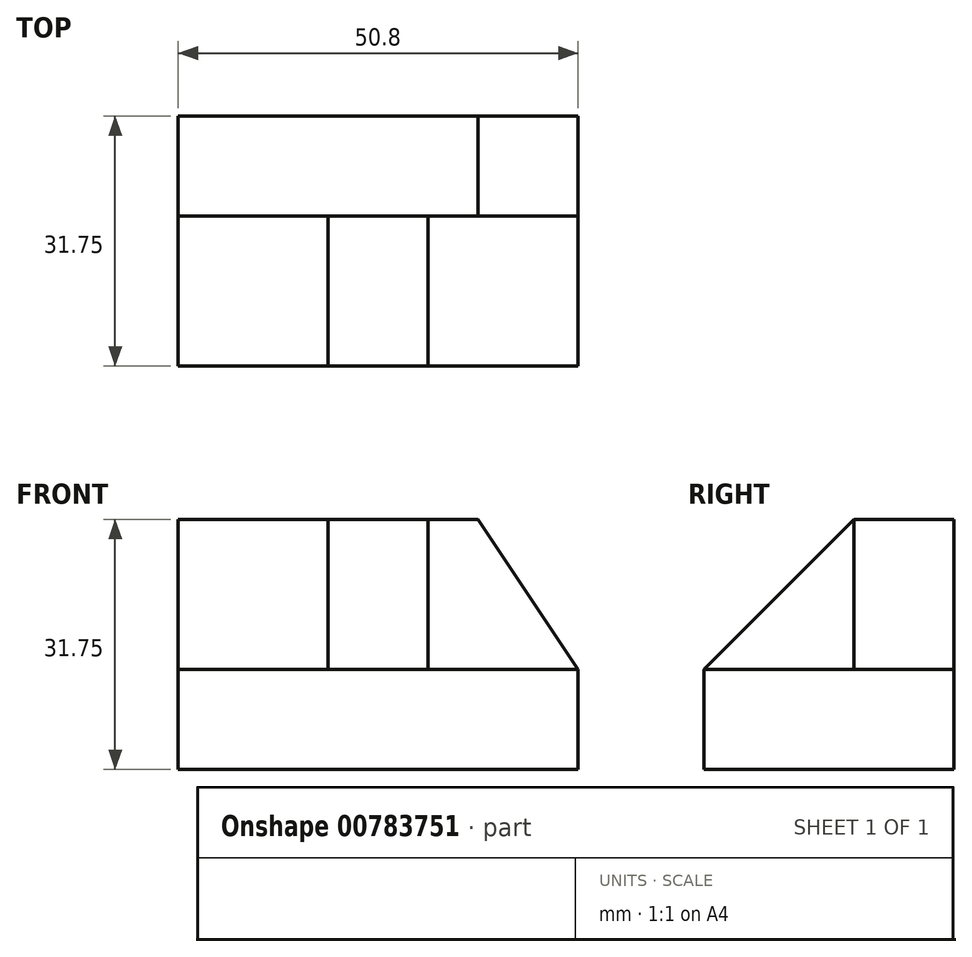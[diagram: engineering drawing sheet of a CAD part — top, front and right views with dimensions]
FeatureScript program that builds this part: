
annotation { "Feature Type Name" : "Feature", "Feature Type Description" : "" }
export const myFeature = defineFeature(function(context is Context, id is Id, definition is map)
    precondition{}
    {
        {
            var Q0;
            Q0=qCreatedBy(makeId("Front.planeOp"),FACE);
            var sketch = newSketch(context, id + "F0", { "sketchPlane" : qUnion([Q0])});
            skLineSegment(sketch, "E0", {"start": v(0, 0) * mm, "end": v(50.8, 0) * mm});
            skLineSegment(sketch, "E1", {"start": v(50.8, 0) * mm, "end": v(50.8, 31.75) * mm});
            skLineSegment(sketch, "E2", {"start": v(50.8, 31.75) * mm, "end": v(0, 31.75) * mm});
            skLineSegment(sketch, "E3", {"start": v(0, 31.75) * mm, "end": v(0, 0) * mm});
            skSolve(sketch);
        }
        {
            var Q0;
            Q0=makeQuery(id+"F0.imprint","IMPRINT",FACE,{"disambiguationData":[TD([[makeQuery(id+"F0.imprint","IMPRINT",EDGE,{"derivedFrom":sQuery(id+"F0.wireOp",EDGE,"E0")}),1.0]])]});
            extrude(context, id + "F1", {"entities" : qUnion([Q0]), "depth" : 31.75 * mm, "offsetDistance" : 25.4 * mm});
        }
        {
            var Q0;
            Q0=makeQuery(id+"F1.opExtrude","SWEPT_FACE",FACE,{"disambiguationData":[OSD([sQuery(id+"F0.wireOp",EDGE,"E3")])]});
            var sketch = newSketch(context, id + "F2", { "sketchPlane" : qUnion([Q0])});
            skLineSegment(sketch, "E4", {"start": v(0, 31.75) * mm, "end": v(12.7, 31.75) * mm});
            skLineSegment(sketch, "E5", {"start": v(31.75, 0) * mm, "end": v(31.75, 12.7) * mm});
            skLineSegment(sketch, "E6", {"start": v(31.75, 12.7) * mm, "end": v(12.7, 12.7) * mm});
            skLineSegment(sketch, "E7", {"start": v(12.7, 12.7) * mm, "end": v(12.7, 31.75) * mm});
            skSolve(sketch);
        }
        {
            var Q0;
            {var subQ0=sQuery(id+"F2.wireOp",EDGE,"E6");Q0=makeQuery(id+"F2.imprint","IMPRINT",FACE,{"disambiguationData":[TD([[makeQuery(id+"F2.imprint","IMPRINT",EDGE,{"derivedFrom":subQ0}),-1.0]])]});}
            extrude(context, id + "F3", {"entities" : qUnion([Q0]), "operationType" : NewBodyOperationType.REMOVE, "oppositeDirection" : true, "depth" : 19.05 * mm, "offsetDistance" : 25.4 * mm});
        }
        {
            var Q0;
            Q0=makeQuery(id+"F1.opExtrude","SWEPT_FACE",FACE,{"disambiguationData":[OSD([sQuery(id+"F0.wireOp",EDGE,"E1")])]});
            var sketch = newSketch(context, id + "F4", { "sketchPlane" : qUnion([Q0])});
            skLineSegment(sketch, "E8", {"start": v(-31.75, 0) * mm, "end": v(-31.75, 12.7) * mm});
            skLineSegment(sketch, "E9", {"start": v(-31.75, 12.7) * mm, "end": v(-12.7, 12.7) * mm});
            skLineSegment(sketch, "E10", {"start": v(0, 31.75) * mm, "end": v(0, 31.75) * mm});
            skLineSegment(sketch, "E11", {"start": v(0, 31.75) * mm, "end": v(-12.7, 31.75) * mm});
            skLineSegment(sketch, "E12", {"start": v(-12.7, 31.75) * mm, "end": v(-12.7, 12.7) * mm});
            skSolve(sketch);
        }
        {
            var Q0;
            {var subQ0=sQuery(id+"F4.wireOp",EDGE,"E9");Q0=makeQuery(id+"F4.imprint","IMPRINT",FACE,{"disambiguationData":[TD([[makeQuery(id+"F4.imprint","IMPRINT",EDGE,{"derivedFrom":subQ0}),1.0]])]});}
            extrude(context, id + "F5", {"entities" : qUnion([Q0]), "operationType" : NewBodyOperationType.REMOVE, "oppositeDirection" : true, "depth" : 19.05 * mm, "offsetDistance" : 25.4 * mm});
        }
        {
            var Q0;
            Q0=makeQuery(id+"F5.boolean.opBoolean","COPY",FACE,{"derivedFrom":makeQuery(id+"F5.opExtrude","CAP_FACE",FACE,{"disambiguationData":[OSD([sQuery(id+"F0.wireOp",EDGE,"E1"),sQuery(id+"F0.wireOp",EDGE,"E2"),sQuery(id+"F4.wireOp",EDGE,"E9"),sQuery(id+"F4.wireOp",EDGE,"E12")])],"isStart":false})});
            var sketch = newSketch(context, id + "F6", { "sketchPlane" : qUnion([Q0])});
            skLineSegment(sketch, "E13", {"start": v(-12.7, 31.75) * mm, "end": v(-31.75, 12.7) * mm});
            skSolve(sketch);
        }
        {
            var Q0;
            Q0=makeQuery(id+"F6.imprint","IMPRINT",FACE,{"disambiguationData":[TD([[makeQuery(id+"F6.imprint","IMPRINT",EDGE,{"derivedFrom":sQuery(id+"F6.wireOp",EDGE,"E13")}),-1.0]])]});
            extrude(context, id + "F7", {"entities" : qUnion([Q0]), "operationType" : NewBodyOperationType.REMOVE, "oppositeDirection" : true, "depth" : 12.7 * mm, "offsetDistance" : 25.4 * mm});
        }
        {
            var Q0;
            Q0=makeQuery(id+"F5.boolean.opBoolean","COPY",FACE,{"derivedFrom":makeQuery(id+"F5.opExtrude","SWEPT_FACE",FACE,{"disambiguationData":[OSD([sQuery(id+"F4.wireOp",EDGE,"E12")])]})});
            var sketch = newSketch(context, id + "F8", { "sketchPlane" : qUnion([Q0])});
            skLineSegment(sketch, "E14", {"start": v(31.75, 31.75) * mm, "end": v(38.1, 31.75) * mm});
            skLineSegment(sketch, "E15", {"start": v(38.1, 31.75) * mm, "end": v(50.8, 12.7) * mm});
            skSolve(sketch);
        }
        {
            var Q0;
            {var subQ0=sQuery(id+"F8.wireOp",EDGE,"E15");Q0=makeQuery(id+"F8.imprint","IMPRINT",FACE,{"disambiguationData":[TD([[makeQuery(id+"F8.imprint","IMPRINT",EDGE,{"derivedFrom":subQ0}),1.0]])]});}
            extrude(context, id + "F9", {"entities" : qUnion([Q0]), "operationType" : NewBodyOperationType.REMOVE, "oppositeDirection" : true, "depth" : 12.7 * mm, "offsetDistance" : 25.4 * mm});
        }
    });
